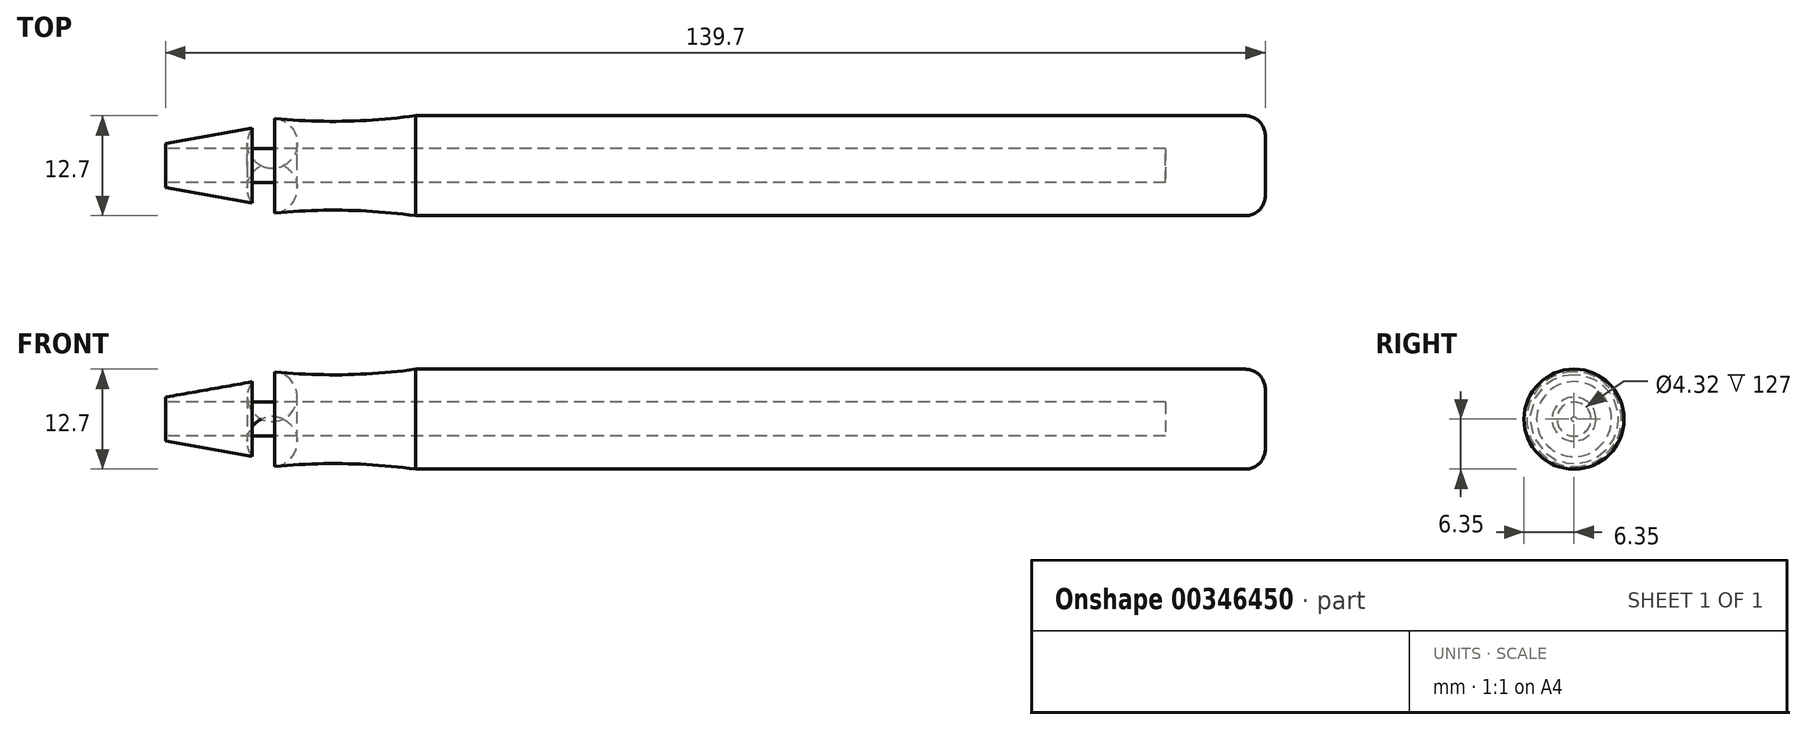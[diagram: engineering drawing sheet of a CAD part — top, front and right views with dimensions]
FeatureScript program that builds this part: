
annotation { "Feature Type Name" : "Feature", "Feature Type Description" : "" }
export const myFeature = defineFeature(function(context is Context, id is Id, definition is map)
    precondition{}
    {
        {
            var Q0;
            Q0=qCreatedBy(makeId("Top.planeOp"),FACE);
            var sketch = newSketch(context, id + "F0", { "sketchPlane" : qUnion([Q0])});
            skLineSegment(sketch, "E0", {"start": v(0, 0) * mm, "end": v(139.7, 0) * mm});
            skLineSegment(sketch, "E1", {"start": v(0, 0) * mm, "end": v(0, 2.8) * mm});
            skLineSegment(sketch, "E2", {"start": v(0, 2.8) * mm, "end": v(11.04, 4.76) * mm});
            skArc(sketch, "E3", {"start": v(11.02, 6.35) * mm, "mid": v(11, 5.56) * mm, "end": v(11.04, 4.76) * mm});
            skArc(sketch, "E4", {"start": v(11.02, 6.35) * mm, "mid": v(21.38, 5.64) * mm, "end": v(31.75, 6.35) * mm});
            skLineSegment(sketch, "E5", {"start": v(31.75, 6.35) * mm, "end": v(139.7, 6.35) * mm});
            skLineSegment(sketch, "E6", {"start": v(139.7, 6.35) * mm, "end": v(139.7, 0) * mm});
            skSolve(sketch);
        }
        {
            var Q0;
            Q0=makeQuery(id+"F0.imprint","IMPRINT",FACE,{"disambiguationData":[TD([[makeQuery(id+"F0.imprint","IMPRINT",EDGE,{"derivedFrom":sQuery(id+"F0.wireOp",EDGE,"E0")}),1.0]])]});
            var Q1;
            Q1=sQuery(id+"F0.wireOp",EDGE,"E0");
            revolve(context, id + "F1", {"entities" : qUnion([Q0]), "axis" : qUnion([Q1]), "revolveType" : RevolveType.FULL});
        }
        {
            var Q0;
            Q0=makeQuery(id+"F1.opRevolve","SWEPT_EDGE",EDGE,{"disambiguationData":[OSD([sQuery(id+"F0.wireOp",EDGE,"E5"),sQuery(id+"F0.wireOp",EDGE,"E6")])]});
            fillet(context, id + "F2", {"entities" : qUnion([Q0]), "radius" : 2.54 * mm, "tangentPropagation" : true, "allowEdgeOverflow" : false});
        }
        {
            var Q0;
            Q0=makeQuery(id+"F1.opRevolve","SWEPT_FACE",FACE,{"disambiguationData":[OSD([sQuery(id+"F0.wireOp",EDGE,"E1")])]});
            var sketch = newSketch(context, id + "F3", { "sketchPlane" : qUnion([Q0])});
            skCircle(sketch, "E7", {"center": v(0, 0) * mm, "radius": 2.16 * mm});
            skSolve(sketch);
        }
        {
            var Q0;
            Q0=makeQuery(id+"F3.imprint","IMPRINT",FACE,{"disambiguationData":[TD([[makeQuery(id+"F3.imprint","IMPRINT",EDGE,{"derivedFrom":sQuery(id+"F3.wireOp",EDGE,"E7")}),1.0]])]});
            extrude(context, id + "F4", {"entities" : qUnion([Q0]), "operationType" : NewBodyOperationType.REMOVE, "oppositeDirection" : true, "depth" : 127 * mm});
        }
        {
            var Q0;
            Q0=makeQuery(id+"F1.opRevolve","SWEPT_EDGE",EDGE,{"disambiguationData":[OSD([sQuery(id+"F0.wireOp",EDGE,"E3"),sQuery(id+"F0.wireOp",EDGE,"E4")])]});
            fillet(context, id + "F5", {"entities" : qUnion([Q0]), "radius" : 3.17 * mm, "tangentPropagation" : true, "allowEdgeOverflow" : false});
        }
    });
